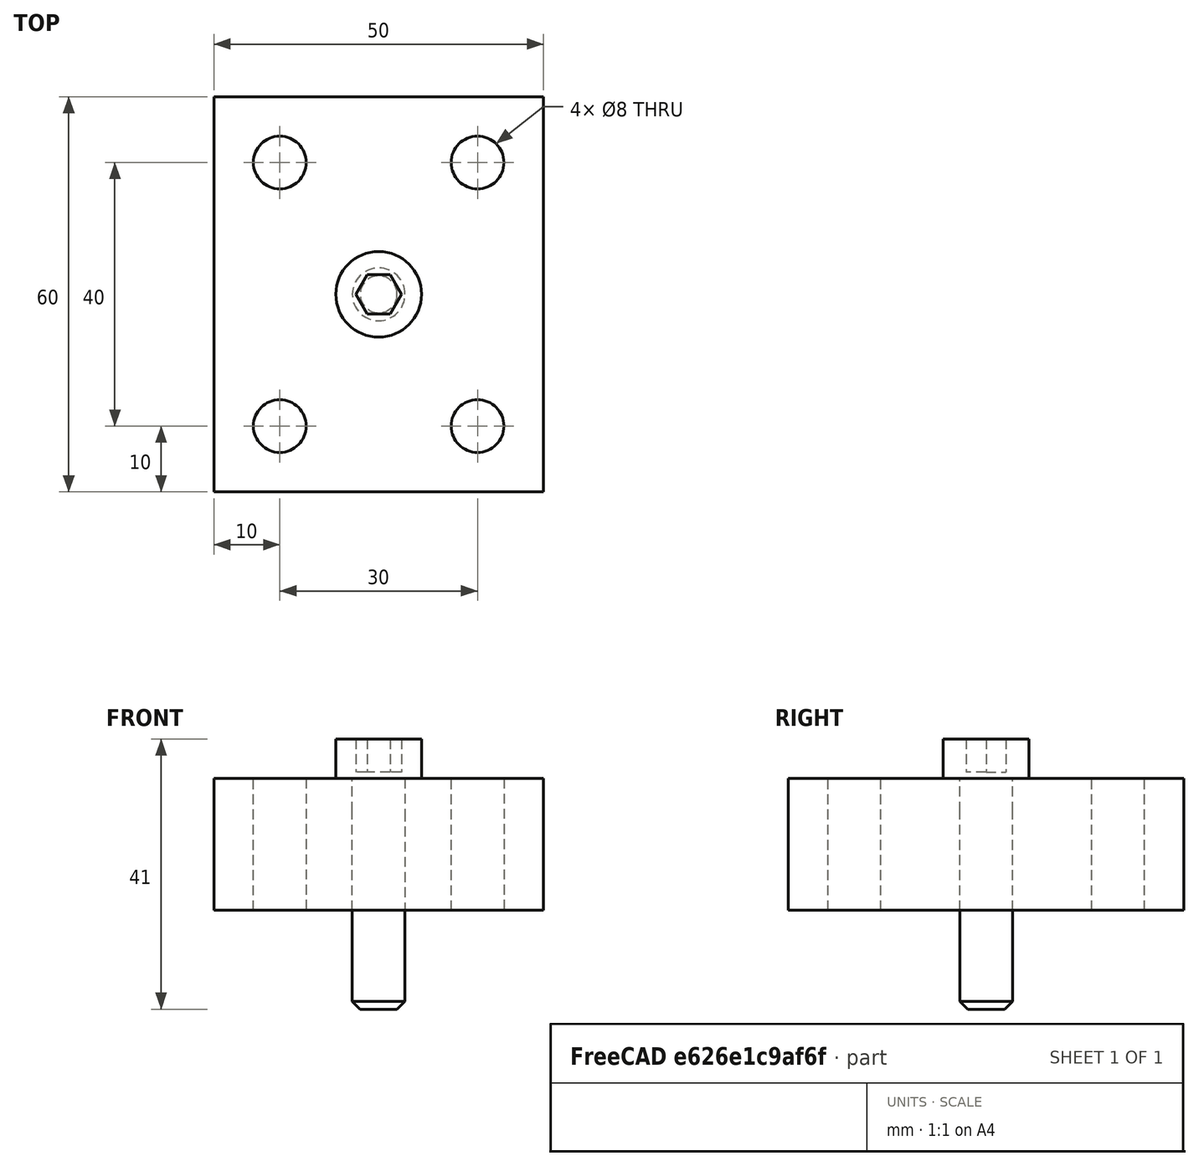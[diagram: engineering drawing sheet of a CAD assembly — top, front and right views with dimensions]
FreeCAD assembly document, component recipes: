
FREECAD ASSEMBLY — COMPONENT RECIPES ("asm3-links-2")

This assembly document has 2 components, labeled P0..P1 below (a component is one placed body or linked part). 2 of them carry a construction recipe — the FreeCAD feature program that regenerates the part from scratch, quoted from this document or its linked companion documents; the rest are supplied as boundary geometry only. No exploded tour is included for this assembly.
COMPONENT P0 — recipe-attached ("Body002", modeled in this document).
Construction recipe (the document's own serialized feature program — sketch geometry with constraints, then the solid features built on it; lengths are millimeters unless a unit is written):

FEATURE [Sketcher::SketchObject] Sketch002
  MapMode = 5
  Support = -> [XY_Plane002]
  sketch-geometry (1):
    g0: Circle CenterX=0 CenterY=0 CenterZ=0 NormalX=0 NormalY=0 NormalZ=1 AngleXU=0 Radius=4
  constraints (2):
    c: Coincident(g0,g-1)
    c: Diameter(g0) = 8  'D1'
FEATURE [PartDesign::Pad] Pad002
  ClaimChildren = false
  Length = 5
  Length2 = 100
  Profile = -> Sketch002
  Reversed = true
  Type = 0
FEATURE [Sketcher::SketchObject] Sketch003
  ExternalGeometry = -> [Pad002]
  MapMode = 5
  Placement = pos=(0,0,-5) rot=(1,0,0;3.14159rad)
  Support = -> [Pad002]
FEATURE [PartDesign::Pad] Pad003
  BaseFeature = -> Pad002
  ClaimChildren = false
  Length = 30
  Length2 = 100
  Profile = -> Sketch003
  Type = 0
  expr: Length = Pad005.Length + 10mm
FEATURE [Sketcher::SketchObject] Sketch004
  MapMode = 5
  Support = -> [XY_Plane002]
  sketch-geometry (1):
    g0: Circle CenterX=0 CenterY=0 CenterZ=0 NormalX=0 NormalY=0 NormalZ=1 AngleXU=0 Radius=6.5
  constraints (2):
    c: Coincident(g0,g-1)
    c: Diameter(g0) = 13  'DH'
FEATURE [PartDesign::Pad] Pad004
  BaseFeature = -> Pad003
  ClaimChildren = false
  Length = 6
  Length2 = 100
  Profile = -> Sketch004
  Type = 0
FEATURE [Sketcher::SketchObject] Sketch005
  MapMode = 5
  Placement = pos=(0,0,6) rot=(0,0,1;0rad)
  Support = -> [Pad004]
  sketch-geometry (7):
    g0: LineSegment StartX=3.4641 StartY=0 StartZ=0 EndX=1.73205 EndY=3 EndZ=0
    g1: LineSegment StartX=1.73205 StartY=3 StartZ=0 EndX=-1.73205 EndY=3 EndZ=0
    g2: LineSegment StartX=-1.73205 StartY=3 StartZ=0 EndX=-3.4641 EndY=0 EndZ=0
    g3: LineSegment StartX=-3.4641 StartY=0 StartZ=0 EndX=-1.73205 EndY=-3 EndZ=0
    g4: LineSegment StartX=-1.73205 StartY=-3 StartZ=0 EndX=1.73205 EndY=-3 EndZ=0
    g5: LineSegment StartX=1.73205 StartY=-3 StartZ=0 EndX=3.4641 EndY=0 EndZ=0
    g6: Circle [constr] CenterX=0 CenterY=0 CenterZ=0 NormalX=0 NormalY=0 NormalZ=1 AngleXU=0 Radius=3.4641
  constraints (16):
    c: Coincident(g0,g1)
    c: Coincident(g1,g2)
    c: Coincident(g2,g3)
    c: Coincident(g3,g4)
    c: Coincident(g4,g5)
    c: Coincident(g5,g0)
    c: Equal(g0, g1-g5) x5
    c: PointOnObject(g0,g6)
    c: PointOnObject(g1,g6)
    c: PointOnObject(g2,g6)
    c: PointOnObject(g3,g6)
    c: PointOnObject(g4,g6)
    c: PointOnObject(g5,g6)
    c: Coincident(g6,g-1)
    c: PointOnObject(g5,g-1)
    c: Distance(g0,g4) = 6  'WS'
FEATURE [PartDesign::Pocket] Pocket
  BaseFeature = -> Pad004
  ClaimChildren = false
  Length = 5
  Length2 = 100
  Profile = -> Sketch005
  Type = 0
FEATURE [PartDesign::Chamfer] Chamfer
  Base = -> Pocket [Edge6]
  BaseFeature = -> Pocket
  Size = 1.2
FEATURE [PartDesign::Body] Body002
  Group = -> [Sketch002,Pad002,Sketch003,Pad003,Sketch004,Pad004,Sketch005,Pocket,Chamfer]
  Origin = -> Origin002
  Tip = -> Chamfer
COMPONENT P1 — recipe-attached ("Body003", modeled in this document).
Construction recipe (the document's own serialized feature program — sketch geometry with constraints, then the solid features built on it; lengths are millimeters unless a unit is written):

FEATURE [Sketcher::SketchObject] Sketch006
  MapMode = 5
  Support = -> [XY_Plane003]
  sketch-geometry (8):
    g0: Circle CenterX=-15 CenterY=20 CenterZ=0 NormalX=0 NormalY=0 NormalZ=1 AngleXU=0 Radius=4
    g1: Circle CenterX=15 CenterY=20 CenterZ=0 NormalX=0 NormalY=0 NormalZ=1 AngleXU=0 Radius=4
    g2: Circle CenterX=15 CenterY=-20 CenterZ=0 NormalX=0 NormalY=0 NormalZ=1 AngleXU=0 Radius=4
    g3: Circle CenterX=-15 CenterY=-20 CenterZ=0 NormalX=0 NormalY=0 NormalZ=1 AngleXU=0 Radius=4
    g4: LineSegment StartX=-25 StartY=30 StartZ=0 EndX=25 EndY=30 EndZ=0
    g5: LineSegment StartX=25 StartY=30 StartZ=0 EndX=25 EndY=-30 EndZ=0
    g6: LineSegment StartX=25 StartY=-30 StartZ=0 EndX=-25 EndY=-30 EndZ=0
    g7: LineSegment StartX=-25 StartY=-30 StartZ=0 EndX=-25 EndY=30 EndZ=0
  constraints (19):
    c: Equal(g0,g1)
    c: Equal(g1,g2)
    c: Equal(g2,g3)
    c: Diameter(g0) = 8  'BHD'
    c: Symmetric(g0,g1,g-2)
    c: Symmetric(g1,g2,g-1)
    c: Symmetric(g0,g3,g-1)
    c: Coincident(g4,g5)
    c: Coincident(g5,g6)
    c: Coincident(g6,g7)
    c: Coincident(g7,g4)
    c: Horizontal(g6)
    c: Vertical(g7)
    c: Symmetric(g4,g4,g-2)
    c: Symmetric(g4,g5,g-1)
    c: Distance(g3,g2) = 30  'L1'
    c: Distance(g4) = 50  'L2'
    c: Distance(g1,g2) = 40  'W1'
    c: Distance(g7) = 60  'W2'
FEATURE [PartDesign::Pad] Pad005
  ClaimChildren = false
  Length = 20
  Length2 = 100
  Profile = -> Sketch006
  Reversed = true
  Type = 0
FEATURE [PartDesign::Body] Body003
  Group = -> [Sketch006,Pad005]
  Origin = -> Origin003
  Tip = -> Pad005
PROVENANCE & LICENSES
A FreeCAD (.FCStd) document from a public repository crawl; recipes are the document's own serialized feature recipes (and, for linked parts, companion documents' recipes).
License: as declared in the source repository (recorded in the dataset sidecar).
